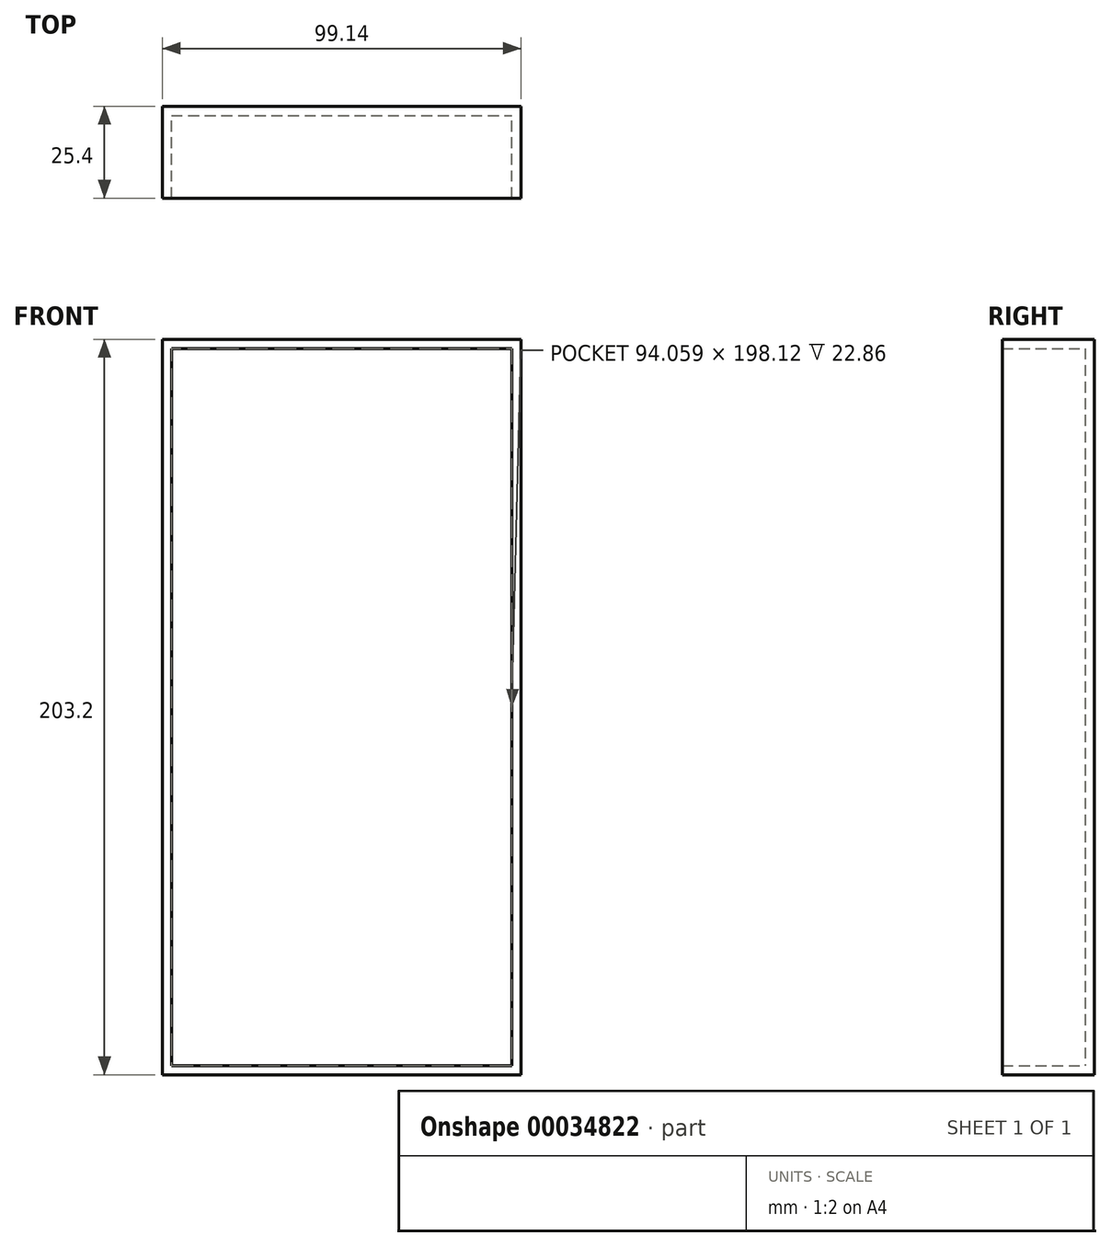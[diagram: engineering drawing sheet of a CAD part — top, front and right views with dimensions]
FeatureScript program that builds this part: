
annotation { "Feature Type Name" : "Feature", "Feature Type Description" : "" }
export const myFeature = defineFeature(function(context is Context, id is Id, definition is map)
    precondition{}
    {
        {
            var Q0;
            Q0=qCreatedBy(makeId("Front.planeOp"),FACE);
            var sketch = newSketch(context, id + "F0", { "sketchPlane" : qUnion([Q0])});
            skLineSegment(sketch, "E0.bottom", {"start": v(-63.43, 123.16) * mm, "end": v(35.71, 123.16) * mm});
            skLineSegment(sketch, "E0.top", {"start": v(-63.43, -80.04) * mm, "end": v(35.71, -80.04) * mm});
            skLineSegment(sketch, "E0.left", {"start": v(-63.43, 123.16) * mm, "end": v(-63.43, -80.04) * mm});
            skLineSegment(sketch, "E0.right", {"start": v(35.71, 123.16) * mm, "end": v(35.71, -80.04) * mm});
            skSolve(sketch);
        }
        {
            var Q0;
            Q0=makeQuery(id+"F0.imprint","IMPRINT",FACE,{"disambiguationData":[TD([[makeQuery(id+"F0.imprint","IMPRINT",EDGE,{"derivedFrom":sQuery(id+"F0.wireOp",EDGE,"E0.bottom")}),-1.0]])]});
            extrude(context, id + "F1", {"entities" : qUnion([Q0]), "depth" : 25.4 * mm});
        }
        {
            var Q0;
            Q0=makeQuery(id+"F1.opExtrude","CAP_FACE",FACE,{"disambiguationData":[OSD([sQuery(id+"F0.wireOp",EDGE,"E0.bottom"),sQuery(id+"F0.wireOp",EDGE,"E0.top"),sQuery(id+"F0.wireOp",EDGE,"E0.left"),sQuery(id+"F0.wireOp",EDGE,"E0.right")])],"isStart":false});
            shell(context, id + "F2", {"entities" : qUnion([Q0]), "thickness" : 2.54 * mm});
        }
    });
